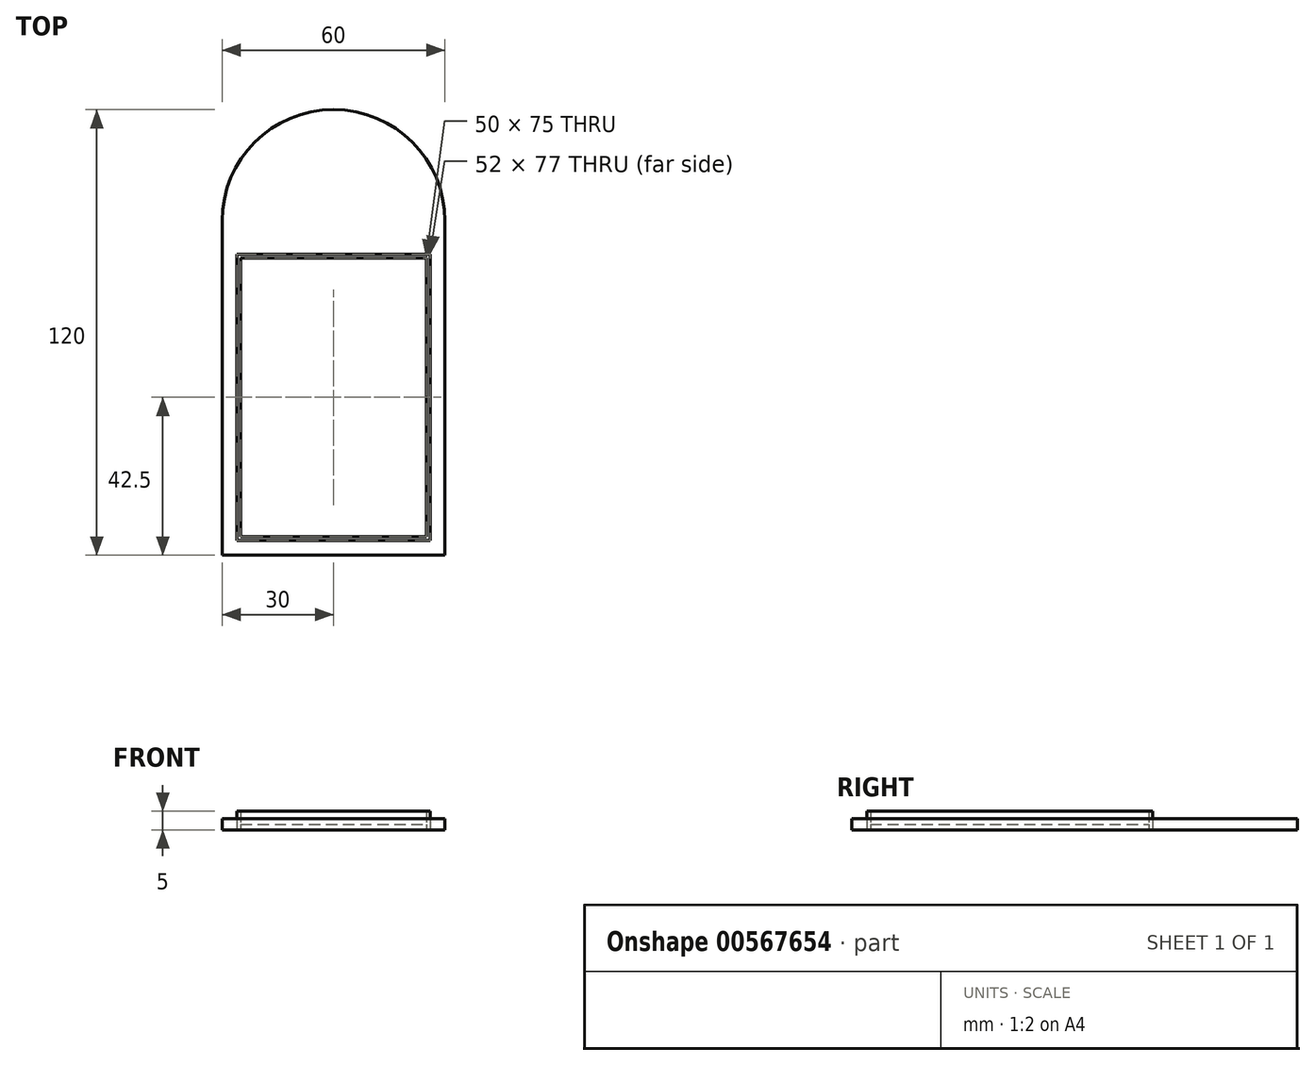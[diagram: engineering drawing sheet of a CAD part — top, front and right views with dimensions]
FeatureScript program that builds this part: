
annotation { "Feature Type Name" : "Feature", "Feature Type Description" : "" }
export const myFeature = defineFeature(function(context is Context, id is Id, definition is map)
    precondition{}
    {
        {
            var Q0;
            Q0=qCreatedBy(makeId("Top.planeOp"),FACE);
            var sketch = newSketch(context, id + "F0", { "sketchPlane" : qUnion([Q0])});
            skLineSegment(sketch, "E0.bottom", {"start": v(0, 0) * mm, "end": v(50, 0) * mm});
            skLineSegment(sketch, "E0.top", {"start": v(0, 75) * mm, "end": v(50, 75) * mm});
            skLineSegment(sketch, "E0.left", {"start": v(0, 0) * mm, "end": v(0, 75) * mm});
            skLineSegment(sketch, "E0.right", {"start": v(50, 0) * mm, "end": v(50, 75) * mm});
            skPoint(sketch, "E1", {"position": v(-5, 0) * mm});
            skLineSegment(sketch, "E2.bottom", {"start": v(0, 0) * mm, "end": v(55, 0) * mm});
            skLineSegment(sketch, "E2.top", {"start": v(-5, 85) * mm, "end": v(55, 85) * mm});
            skLineSegment(sketch, "E2.left", {"start": v(-5, 0) * mm, "end": v(-5, 85) * mm});
            skLineSegment(sketch, "E2.right", {"start": v(55, 0) * mm, "end": v(55, 85) * mm});
            skArc(sketch, "E3", {"start": v(55, 85) * mm, "mid": v(25, 115) * mm, "end": v(-5, 85) * mm});
            skPoint(sketch, "E4", {"position": v(25, 115) * mm});
            skLineSegment(sketch, "E5.top", {"start": v(-5, -5) * mm, "end": v(55, -5) * mm});
            skLineSegment(sketch, "E5.left", {"start": v(-5, 0) * mm, "end": v(-5, -5) * mm});
            skLineSegment(sketch, "E5.right", {"start": v(55, 0) * mm, "end": v(55, -5) * mm});
            skPoint(sketch, "E6", {"position": v(0, 37.5) * mm});
            skPoint(sketch, "E7", {"position": v(25, 75) * mm});
            skPoint(sketch, "E8", {"position": v(50, 37.5) * mm});
            skPoint(sketch, "E9", {"position": v(25, 0) * mm});
            skLineSegment(sketch, "E10.bottom", {"start": v(-1, 76) * mm, "end": v(51, 76) * mm});
            skLineSegment(sketch, "E10.top", {"start": v(-1, -1) * mm, "end": v(51, -1) * mm});
            skLineSegment(sketch, "E10.left", {"start": v(-1, 76) * mm, "end": v(-1, -1) * mm});
            skLineSegment(sketch, "E10.right", {"start": v(51, 76) * mm, "end": v(51, -1) * mm});
            skPoint(sketch, "E10.middle", {"position": v(25, 37.5) * mm});
            skSolve(sketch);
        }
        {
            var Q0;
            Q0=makeQuery(id+"F0.imprint","IMPRINT",FACE,{"disambiguationData":[TD([[makeQuery(id+"F0.imprint","IMPRINT",EDGE,{"derivedFrom":sQuery(id+"F0.wireOp",EDGE,"E2.top")}),-1.0]])]});
            var Q1;
            Q1=makeQuery(id+"F0.imprint","IMPRINT",FACE,{"disambiguationData":[TD([[makeQuery(id+"F0.imprint","IMPRINT",EDGE,{"derivedFrom":sQuery(id+"F0.wireOp",EDGE,"E2.top")}),1.0]])]});
            extrude(context, id + "F1", {"entities" : qUnion([Q0, Q1]), "depth" : 3 * mm, "offsetDistance" : 25 * mm});
        }
        {
            var Q0;
            Q0=makeQuery(id+"F0.imprint","IMPRINT",FACE,{"disambiguationData":[TD([[makeQuery(id+"F0.imprint","IMPRINT",EDGE,{"derivedFrom":sQuery(id+"F0.wireOp",EDGE,"E0.top")}),-1.0]])]});
            extrude(context, id + "F2", {"entities" : qUnion([Q0]), "operationType" : NewBodyOperationType.ADD, "depth" : 1.5 * mm, "offsetDistance" : 25 * mm});
        }
        {
            var Q0;
            Q0=makeQuery(id+"F0.imprint","IMPRINT",FACE,{"disambiguationData":[TD([[makeQuery(id+"F0.imprint","IMPRINT",EDGE,{"derivedFrom":sQuery(id+"F0.wireOp",EDGE,"E0.top")}),1.0]])]});
            extrude(context, id + "F3", {"entities" : qUnion([Q0]), "depth" : 5 * mm, "offsetDistance" : 25 * mm});
        }
    });
